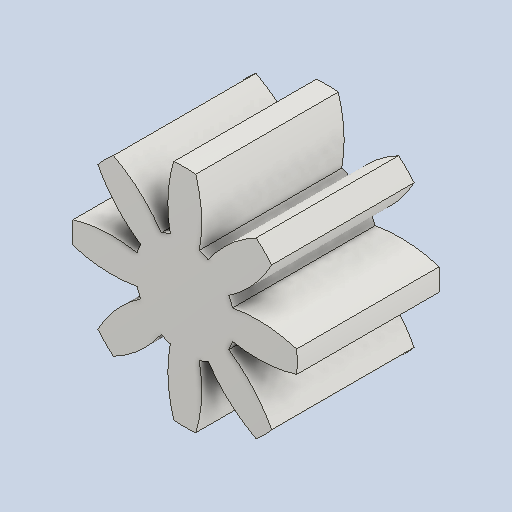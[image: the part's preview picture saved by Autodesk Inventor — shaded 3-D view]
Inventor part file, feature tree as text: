
AUTODESK INVENTOR PART (.ipt)
format: ipt  version: 2023.1 (Build 271208000, 208)  size: 195,584 bytes
history: native  units: mm (DEFAULTED — no unit token found)
features: plane x3, other x3, sketch x2, extrude x1
ambient origin geometry x8: Origin, YZ Plane, XZ Plane, XY Plane, X Axis, Y Axis, Z Axis, Center Point
bodies: Solid1 (feature_tree)
feature tree (9):
  extrude  "Extrusion1"  Depth=10.0mm TaperAngle=0.0deg
  plane  "Work Plane2"
  plane  "Work Plane8"
  plane  "Work Plane9"
  other  "Spur Gear"
  sketch  "Sketch1"  dims[d0=15.785039mm d1=10.0mm d2=0.0mm]
  sketch  "Sketch2"  dims[d3=12.0mm d4=10.0mm d5=0.0mm d16=30.0mm d17=0.0mm d34=22.5deg d39=0.0mm d41=0.0mm d43=30.0mm d46=30.0mm d47=0.0mm d48=0.0mm]
  other  "Srf1"
  other  "Pitch Diameter"
